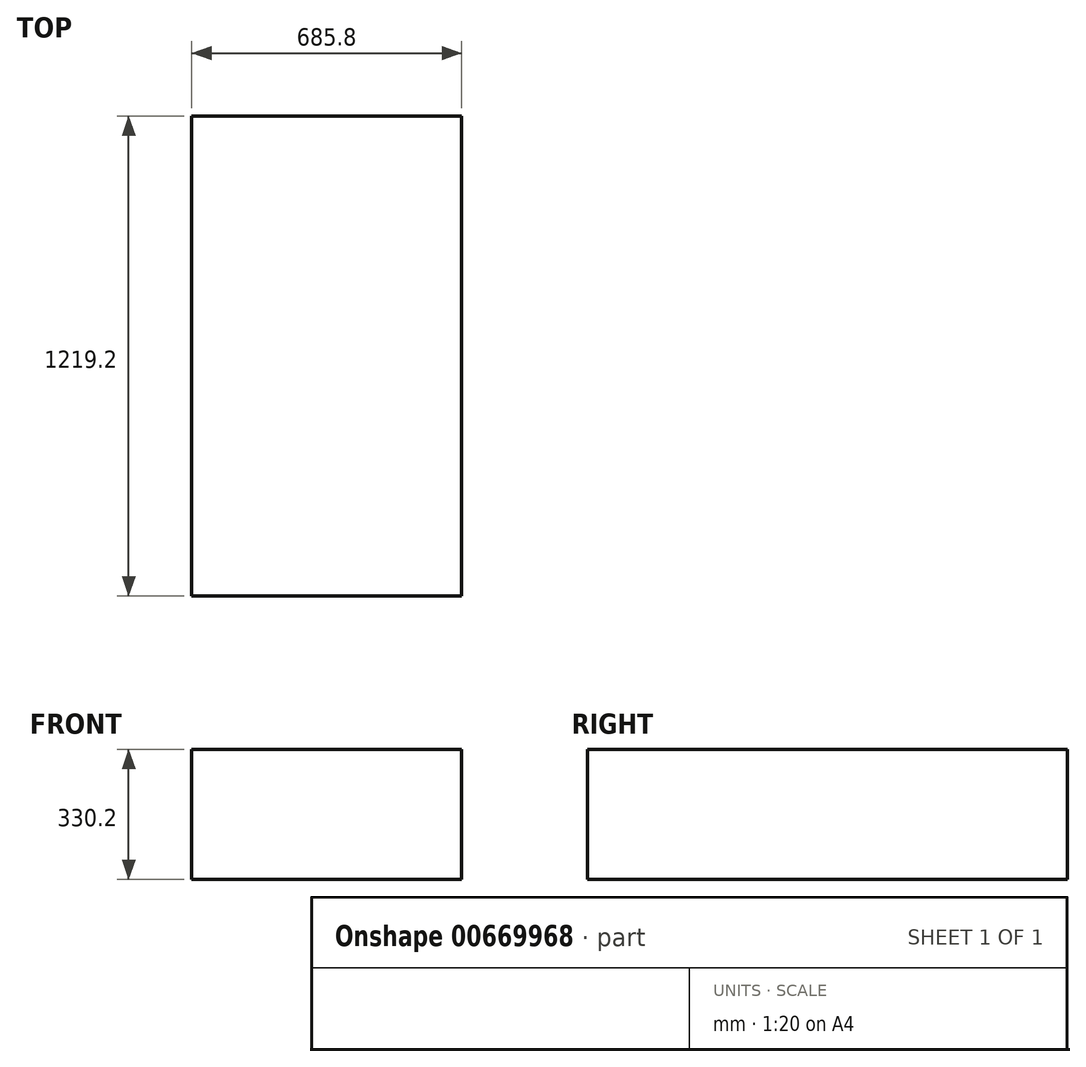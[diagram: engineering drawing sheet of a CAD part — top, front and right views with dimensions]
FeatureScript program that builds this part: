
annotation { "Feature Type Name" : "Feature", "Feature Type Description" : "" }
export const myFeature = defineFeature(function(context is Context, id is Id, definition is map)
    precondition{}
    {
        {
            var Q0;
            Q0=qCreatedBy(makeId("Top.planeOp"),FACE);
            var sketch = newSketch(context, id + "F0", { "sketchPlane" : qUnion([Q0])});
            skLineSegment(sketch, "E0.bottom", {"start": v(342.9, 609.6) * mm, "end": v(-342.9, 609.6) * mm});
            skLineSegment(sketch, "E0.top", {"start": v(342.9, -609.6) * mm, "end": v(-342.9, -609.6) * mm});
            skLineSegment(sketch, "E0.left", {"start": v(342.9, 609.6) * mm, "end": v(342.9, -609.6) * mm});
            skLineSegment(sketch, "E0.right", {"start": v(-342.9, 609.6) * mm, "end": v(-342.9, -609.6) * mm});
            skPoint(sketch, "E0.middle", {"position": v(0, 0) * mm});
            skSolve(sketch);
        }
        {
            var Q0;
            Q0=makeQuery(id+"F0.imprint","IMPRINT",FACE,{"disambiguationData":[TD([[makeQuery(id+"F0.imprint","IMPRINT",EDGE,{"derivedFrom":sQuery(id+"F0.wireOp",EDGE,"E0.bottom")}),1.0]])]});
            extrude(context, id + "F1", {"entities" : qUnion([Q0]), "depth" : 330.2 * mm, "offsetDistance" : 25.4 * mm});
        }
    });
